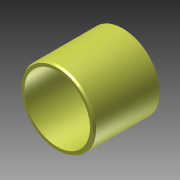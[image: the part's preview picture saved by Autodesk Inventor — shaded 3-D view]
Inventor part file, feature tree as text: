
AUTODESK INVENTOR PART (.ipt)
format: ipt  version: 2011 (Build 150239000, 239)  size: 94,720 bytes
history: native  units: mm
features: chamfer x2, sketch x1
ambient origin geometry x8: Origin, YZ Plane, XZ Plane, XY Plane, X Axis, Y Axis, Z Axis, Center Point
bodies: Solid1 (feature_tree), Body (feature_tree)
feature tree (3):
  chamfer  "Chamfer - Outside"  Distance=25.4mm
  chamfer  "Chamfer - Inside"  Distance=25.4mm
  sketch  "Sketch1"  dims[d0=28.575mm d1=25.4mm d2=0.0mm d3=25.4mm d4=25.4mm d5=25.4mm d6=12.7mm d7=9.525mm d8=6.35mm d9=14.3117mm d10=19.05mm d11=20.594885mm d12=0.7874mm d13=3.175mm d14=30.0deg d15=0.7874mm d16=3.175mm d17=30.0deg]
